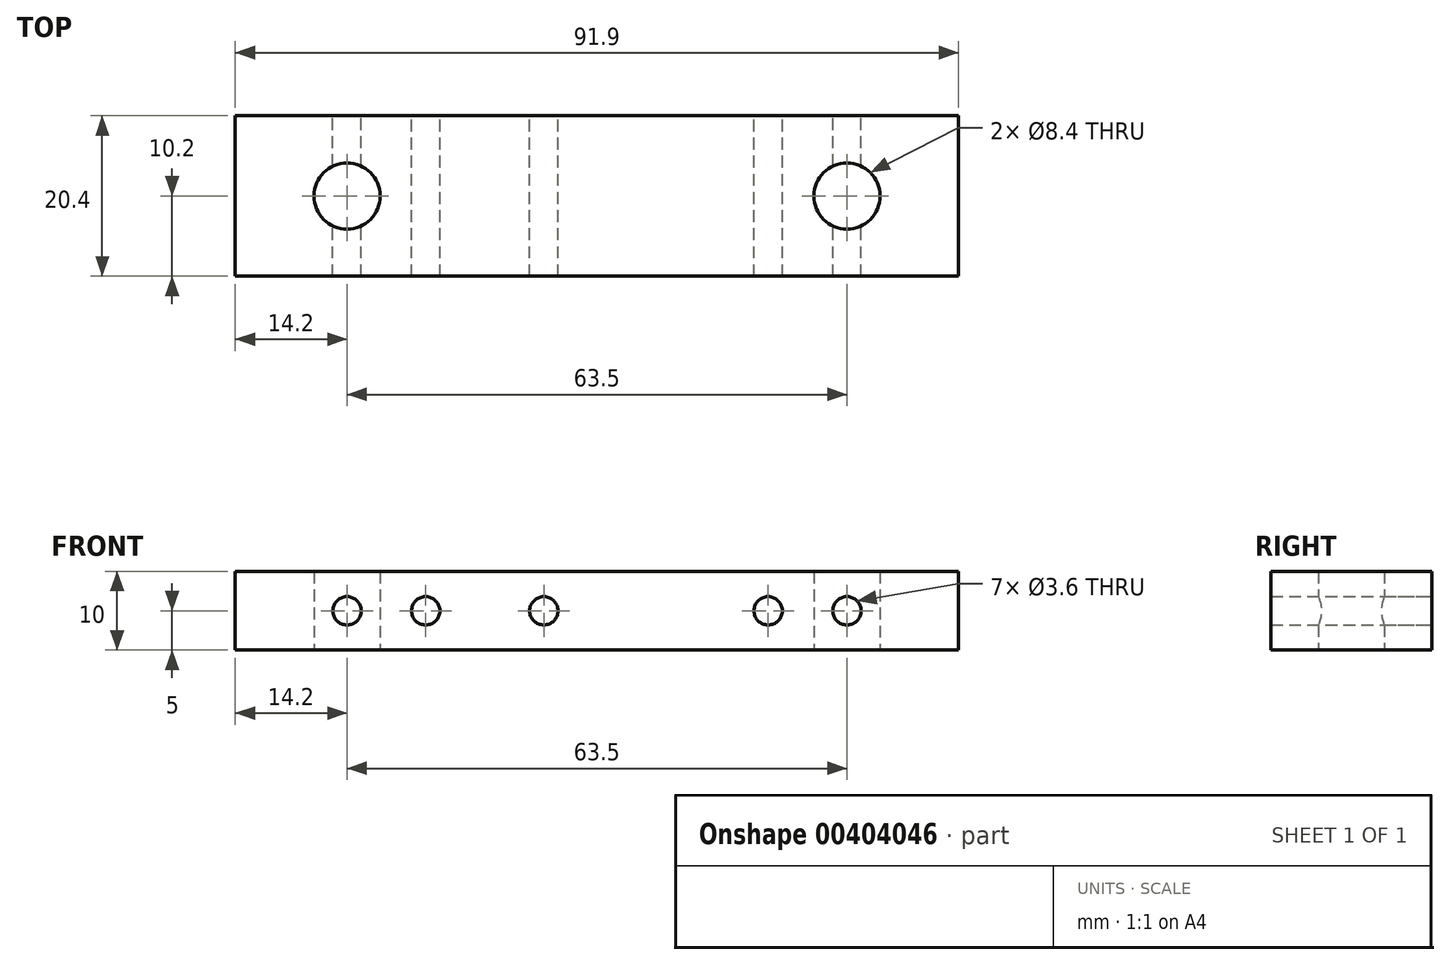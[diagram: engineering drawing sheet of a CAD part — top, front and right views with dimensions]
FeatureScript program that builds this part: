
annotation { "Feature Type Name" : "Feature", "Feature Type Description" : "" }
export const myFeature = defineFeature(function(context is Context, id is Id, definition is map)
    precondition{}
    {
        {
            var Q0;
            Q0=qCreatedBy(makeId("Top.planeOp"),FACE);
            var sketch = newSketch(context, id + "F0", { "sketchPlane" : qUnion([Q0])});
            skLineSegment(sketch, "E0.bottom", {"start": v(-45.95, 10.2) * mm, "end": v(45.95, 10.2) * mm});
            skLineSegment(sketch, "E0.top", {"start": v(-45.95, -10.2) * mm, "end": v(45.95, -10.2) * mm});
            skLineSegment(sketch, "E0.left", {"start": v(-45.95, 10.2) * mm, "end": v(-45.95, -10.2) * mm});
            skLineSegment(sketch, "E0.right", {"start": v(45.95, 10.2) * mm, "end": v(45.95, -10.2) * mm});
            skCircle(sketch, "E1", {"center": v(-31.75, 0) * mm, "radius": 4.2 * mm});
            skCircle(sketch, "E2", {"center": v(31.75, 0) * mm, "radius": 4.2 * mm});
            skLineSegment(sketch, "E3", {"start": v(31.75, 0) * mm, "end": v(0, 0) * mm, "construction": true});
            skLineSegment(sketch, "E4", {"start": v(0, 0) * mm, "end": v(-31.75, 0) * mm, "construction": true});
            skLineSegment(sketch, "E5", {"start": v(-45.95, 0) * mm, "end": v(-35.95, 0) * mm, "construction": true});
            skLineSegment(sketch, "E6", {"start": v(-31.75, 0) * mm, "end": v(-31.75, 4.2) * mm, "construction": true});
            skLineSegment(sketch, "E7", {"start": v(-31.75, 4.2) * mm, "end": v(-31.75, 10.2) * mm});
            skSolve(sketch);
        }
        {
            var Q0;
            Q0=makeQuery(id+"F0.imprint","IMPRINT",FACE,{"disambiguationData":[TD([[makeQuery(id+"F0.imprint","IMPRINT",EDGE,{"derivedFrom":sQuery(id+"F0.wireOp",EDGE,"E0.top")}),1.0]])]});
            extrude(context, id + "F1", {"entities" : qUnion([Q0]), "depth" : 10 * mm});
        }
        {
            var Q0;
            Q0=makeQuery(id+"F1.opExtrude","SWEPT_FACE",FACE,{"disambiguationData":[OSD([sQuery(id+"F0.wireOp",EDGE,"E0.bottom")])]});
            var sketch = newSketch(context, id + "F2", { "sketchPlane" : qUnion([Q0])});
            skLineSegment(sketch, "E8.0", {"start": v(27.55, 10) * mm, "end": v(35.95, 10) * mm, "construction": true});
            skLineSegment(sketch, "E8.1", {"start": v(-35.95, 10) * mm, "end": v(-27.55, 10) * mm, "construction": true});
            skLineSegment(sketch, "E9", {"start": v(-31.75, 10) * mm, "end": v(-31.75, 0) * mm, "construction": true});
            skLineSegment(sketch, "E10", {"start": v(31.75, 10) * mm, "end": v(31.75, 0) * mm, "construction": true});
            skPoint(sketch, "E11", {"position": v(-31.75, 5) * mm});
            skPoint(sketch, "E12", {"position": v(31.75, 5) * mm});
            skLineSegment(sketch, "E13", {"start": v(-31.75, 5) * mm, "end": v(-21.75, 5) * mm, "construction": true});
            skLineSegment(sketch, "E14", {"start": v(31.75, 5) * mm, "end": v(21.75, 5) * mm, "construction": true});
            skLineSegment(sketch, "E15", {"start": v(21.75, 5) * mm, "end": v(6.75, 5) * mm, "construction": true});
            skSolve(sketch);
        }
        {
            var Q0;
            Q0=sQuery(id+"F2.wireOp",VERTEX,"E11");
            var Q1;
            Q1=sQuery(id+"F2.wireOp",VERTEX,"E13.end");
            var Q2;
            Q2=sQuery(id+"F2.wireOp",VERTEX,"E14.end");
            var Q3;
            Q3=sQuery(id+"F2.wireOp",VERTEX,"E12");
            var Q4;
            Q4=sQuery(id+"F2.wireOp",VERTEX,"E15.end");
            var Q5;
            Q5=makeQuery(id+"F1.opExtrude","SWEPT_BODY",BODY,{"disambiguationData":[OSD([sQuery(id+"F0.wireOp",EDGE,"E0.bottom"),sQuery(id+"F0.wireOp",EDGE,"E0.top"),sQuery(id+"F0.wireOp",EDGE,"E0.left"),sQuery(id+"F0.wireOp",EDGE,"E0.right"),sQuery(id+"F0.wireOp",EDGE,"E1"),sQuery(id+"F0.wireOp",EDGE,"E2")])]});
            hole(context, id + "F3", {"style" : HoleStyle.SIMPLE, "endStyle" : HoleEndStyle.THROUGH, "holeDiameter" : 3.6 * mm, "isTappedThrough" : true, "tappedDepth" : 12 * mm, "tapClearance" : 3, "startFromSketch" : true, "locations" : qUnion([Q0, Q1, Q2, Q3, Q4]), "scope" : qUnion([Q5])});
        }
    });
